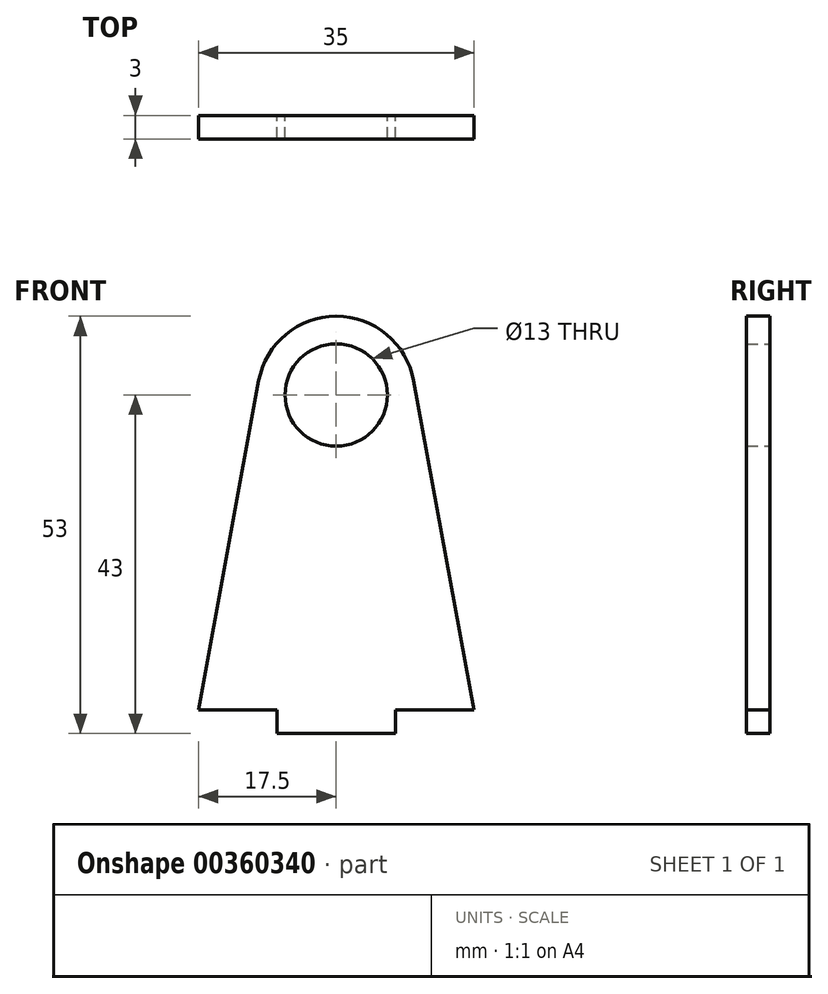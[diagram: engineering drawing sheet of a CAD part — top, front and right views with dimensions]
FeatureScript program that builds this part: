
annotation { "Feature Type Name" : "Feature", "Feature Type Description" : "" }
export const myFeature = defineFeature(function(context is Context, id is Id, definition is map)
    precondition{}
    {
        {
            var Q0;
            Q0=qCreatedBy(makeId("Front.planeOp"),FACE);
            var sketch = newSketch(context, id + "F0", { "sketchPlane" : qUnion([Q0])});
            skLineSegment(sketch, "E0", {"start": v(-9.84, 41.8) * mm, "end": v(-17.5, 0) * mm});
            skLineSegment(sketch, "E1", {"start": v(-17.5, 0) * mm, "end": v(-7.5, 0) * mm});
            skLineSegment(sketch, "E2", {"start": v(-7.5, 0) * mm, "end": v(-7.5, -3) * mm});
            skArc(sketch, "E3", {"start": v(-9.84, 41.8) * mm, "mid": v(-6.4, 47.68) * mm, "end": v(0, 50) * mm});
            skLineSegment(sketch, "E4", {"start": v(-7.5, -3) * mm, "end": v(0, -3) * mm});
            skArc(sketch, "E5", {"start": v(0, 46.5) * mm, "mid": v(-6.5, 40) * mm, "end": v(0, 33.5) * mm});
            skLineSegment(sketch, "E6.MirrorCS", {"start": v(7.5, -3) * mm, "end": v(0, -3) * mm});
            skLineSegment(sketch, "E7.MirrorCS", {"start": v(7.5, 0) * mm, "end": v(7.5, -3) * mm});
            skLineSegment(sketch, "E8.MirrorCS", {"start": v(9.84, 41.8) * mm, "end": v(17.5, 0) * mm});
            skLineSegment(sketch, "E9.MirrorCS", {"start": v(17.5, 0) * mm, "end": v(7.5, 0) * mm});
            skArc(sketch, "E10.MirrorCS", {"start": v(9.84, 41.8) * mm, "mid": v(6.4, 47.68) * mm, "end": v(0, 50) * mm});
            skArc(sketch, "E11.MirrorCS", {"start": v(0, 46.5) * mm, "mid": v(6.5, 40) * mm, "end": v(0, 33.5) * mm});
            skSolve(sketch);
        }
        {
            var Q0;
            Q0 = qSketchRegion(id + "F0", true);
            extrude(context, id + "F1", {"entities" : qUnion([Q0]), "depth" : 3 * mm});
        }
    });
